# Revit family: Furniture_Other-Furniture_Midmark_Wall-Hung-Base-Cabinetry__
name_source: partatom
category: Casework
units: mm (PartAtom-declared; Revit-internal decimal feet)

## family parameters
Cut with Voids When Loaded = No
Host = Face
Room Calculation Point = No
Shared = No

## types (1)
- Default - Please Load Revit Family Type Catalog
    Cabinet Finish = Wood - Midmark - Storm
    Default Elevation = 2' - 10 1/2"
    Depth = 1' - 6"
    Description = Synthesis Cabinetry offers multiple storage options designed to fit your needs, for both today and tomorrow. Traditional and wall-hung base cabinets are available in a multitude of door and drawer configurations to help you create the perfect storage solution for your facility.
    Door Drawer Configuration = Door Drawer Options : RH Door
    Height = 1' - 7"
    Manufacturer = Midmark
    Model = BG02 - RH Door - 24x19
    Product Guid = b197bfa6-cea0-4ad1-b350-2ef8ecfbbb1e
    Product Page URL = https://www.midmark.com
    Product data url = https://www.bimobject.com
    Shelves = Yes
    URL = https://www.midmark.com
    Width = 2' - 0"

## geometry (parser evidence)
native form markers: Blend x2, Sweep x7
no freeform markers — native parametric forms only
